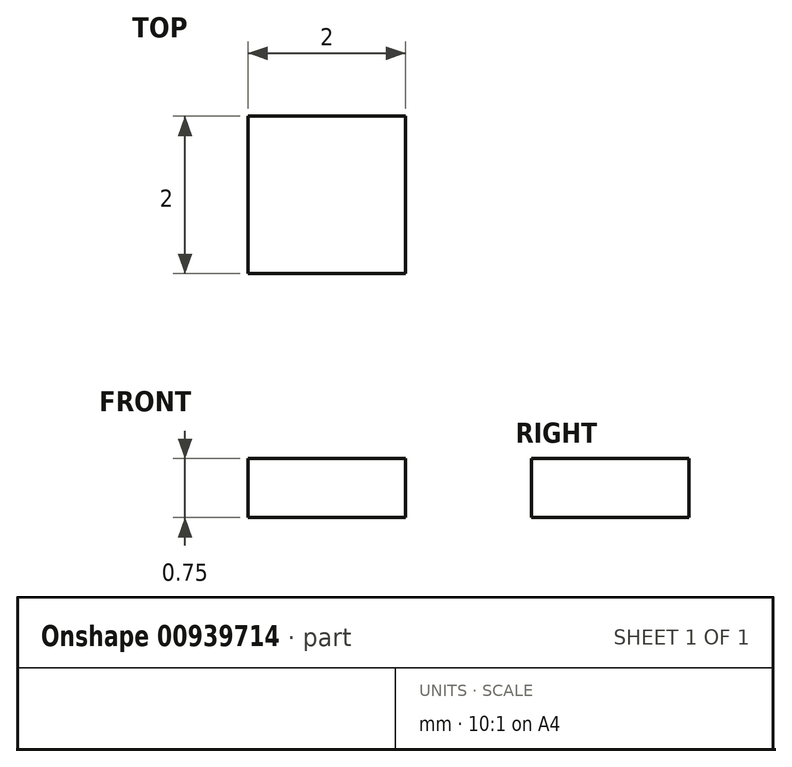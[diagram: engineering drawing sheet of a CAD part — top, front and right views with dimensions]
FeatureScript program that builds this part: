
annotation { "Feature Type Name" : "Feature", "Feature Type Description" : "" }
export const myFeature = defineFeature(function(context is Context, id is Id, definition is map)
    precondition{}
    {
        {
            var Q0;
            Q0=qCreatedBy(makeId("Top.planeOp"),FACE);
            var sketch = newSketch(context, id + "F0", { "sketchPlane" : qUnion([Q0])});
            skLineSegment(sketch, "E0.bottom", {"start": v(-1, 1) * mm, "end": v(1, 1) * mm});
            skLineSegment(sketch, "E0.top", {"start": v(-1, -1) * mm, "end": v(1, -1) * mm});
            skLineSegment(sketch, "E0.left", {"start": v(-1, 1) * mm, "end": v(-1, -1) * mm});
            skLineSegment(sketch, "E0.right", {"start": v(1, 1) * mm, "end": v(1, -1) * mm});
            skSolve(sketch);
        }
        {
            var Q0;
            Q0 = qSketchRegion(id + "F0", true);
            extrude(context, id + "F1", {"entities" : qUnion([Q0]), "depth" : 0.75 * mm, "offsetDistance" : 25 * mm});
        }
    });
